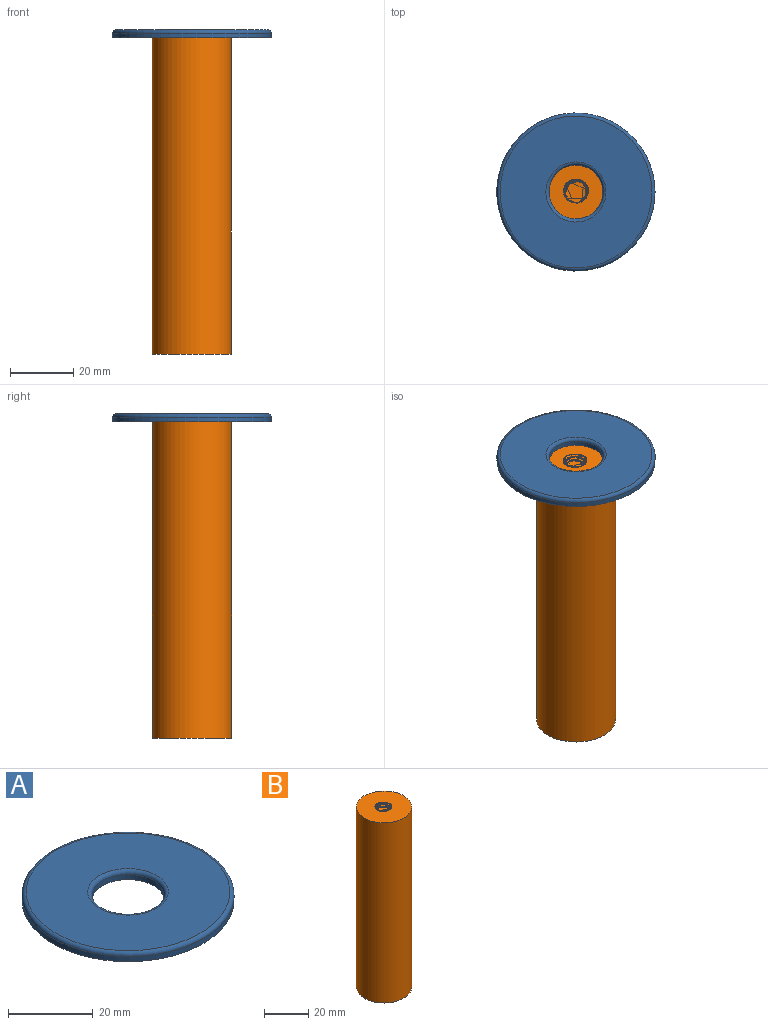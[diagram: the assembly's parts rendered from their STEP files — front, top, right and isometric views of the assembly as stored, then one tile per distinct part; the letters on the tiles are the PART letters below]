
ASSEMBLY  parts=2 mates=1
PART A: 6 faces, bbox 54.1x54.1x2.5 mm
  f0: cylinder r=8.5mm len=17mm, axis (0,0,-1), area 80.1mm2, adj f3,f4
  f1: cylinder r=25mm len=50mm, axis (0,0,-1), area 235.6mm2, adj f3,f5
  f2: plane 48x48mm, normal (0,0,1), area 1526mm2, adj f4,f5
  f3: plane 50x50mm, normal (0,0,-1), area 1736.5mm2, adj f0,f1
  f4: torus R=9.5mm, axis (0,0,1), area 87.5mm2, adj f0,f2
  f5: torus R=24mm, axis (0,0,1), area 243.2mm2, adj f1,f2
PART B: 8 faces, bbox 25.4x25.4x100.9 mm
  f0: plane 7.7x7.69mm, normal (0,0,1), area 42.6mm2, adj f4,f5,f6,f7
  f1: plane 25.36x25.36mm, normal (0,0,1), area 448.2mm2, adj f2,f4,f5,f6,f7
  f2: cylinder r=12.5mm len=100mm, axis (0,0,-1), area 7854mm2, adj f1,f3
  f3: plane 25x25mm, normal (0,0,-1), area 490.9mm2, adj f2
  f4: bspline ~25.81x9.36mm, area 362.7mm2, adj f0,f1,f6,f7
  f5: bspline ~26.02x9.36mm, area 366.4mm2, adj f0,f1,f6,f7
  f6: bspline ~25.57x9.49mm, area 92.5mm2, adj f0,f1,f4,f5
  f7: cylinder r=3.38mm len=25mm, axis (0,0,-1), area 307.5mm2, adj f0,f1,f4,f5
PLACE A t=(0,0,100)mm
PLACE B at identity
MATE planar A.f1 <-> B.f2  axis (0,0,1) through (0,0,102.5)mm
